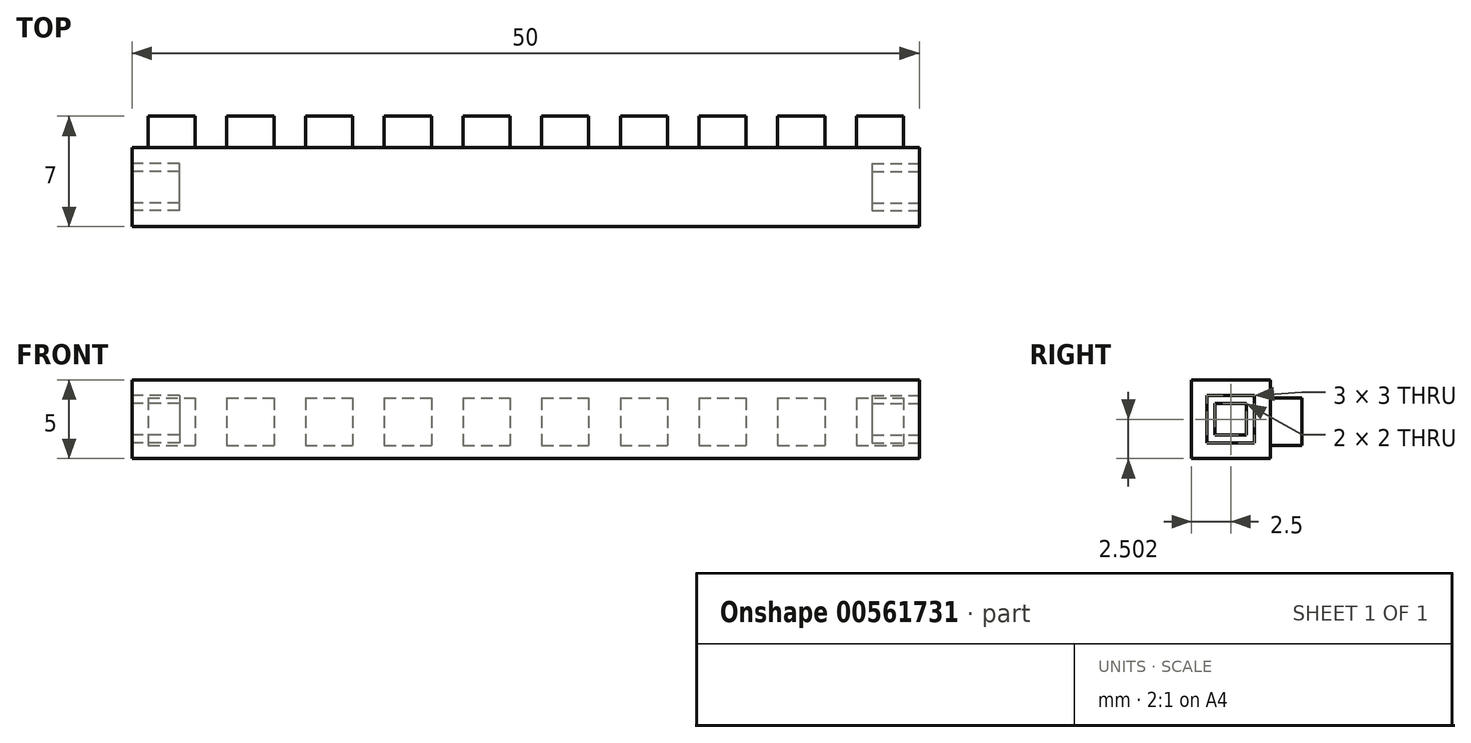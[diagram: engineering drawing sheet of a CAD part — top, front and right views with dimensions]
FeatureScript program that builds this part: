
annotation { "Feature Type Name" : "Feature", "Feature Type Description" : "" }
export const myFeature = defineFeature(function(context is Context, id is Id, definition is map)
    precondition{}
    {
        {
            var Q0;
            Q0=qCreatedBy(makeId("Front.planeOp"),FACE);
            var sketch = newSketch(context, id + "F0", { "sketchPlane" : qUnion([Q0])});
            skLineSegment(sketch, "E0", {"start": v(-35.48, 11.23) * mm, "end": v(-35.48, 6.23) * mm});
            skLineSegment(sketch, "E1", {"start": v(-35.48, 6.23) * mm, "end": v(14.52, 6.23) * mm});
            skLineSegment(sketch, "E2", {"start": v(14.52, 6.23) * mm, "end": v(14.52, 11.23) * mm});
            skLineSegment(sketch, "E3", {"start": v(14.52, 11.23) * mm, "end": v(-35.48, 11.23) * mm});
            skSolve(sketch);
        }
        {
            var Q0;
            Q0=makeQuery(id+"F0.imprint","IMPRINT",FACE,{"disambiguationData":[TD([[makeQuery(id+"F0.imprint","IMPRINT",EDGE,{"derivedFrom":sQuery(id+"F0.wireOp",EDGE,"E0")}),1.0]])]});
            extrude(context, id + "F1", {"entities" : qUnion([Q0]), "depth" : 5 * mm, "offsetDistance" : 25 * mm});
        }
        {
            var Q0;
            Q0=qCreatedBy(makeId("Front.planeOp"),FACE);
            var sketch = newSketch(context, id + "F2", { "sketchPlane" : qUnion([Q0])});
            skLineSegment(sketch, "E4.bottom", {"start": v(-34.48, 10.09) * mm, "end": v(-31.48, 10.09) * mm});
            skLineSegment(sketch, "E4.top", {"start": v(-34.48, 7.09) * mm, "end": v(-31.48, 7.09) * mm});
            skLineSegment(sketch, "E4.left", {"start": v(-34.48, 10.09) * mm, "end": v(-34.48, 7.09) * mm});
            skLineSegment(sketch, "E4.right", {"start": v(-31.48, 10.09) * mm, "end": v(-31.48, 7.09) * mm});
            skPoint(sketch, "E4.middle", {"position": v(-32.98, 8.59) * mm});
            skLineSegment(sketch, "E5.1.0.0", {"start": v(-29.48, 10.09) * mm, "end": v(-26.48, 10.09) * mm});
            skLineSegment(sketch, "E5.1.0.1", {"start": v(-29.48, 10.09) * mm, "end": v(-29.48, 7.09) * mm});
            skLineSegment(sketch, "E5.1.0.2", {"start": v(-29.48, 7.09) * mm, "end": v(-26.48, 7.09) * mm});
            skLineSegment(sketch, "E5.1.0.3", {"start": v(-26.48, 10.09) * mm, "end": v(-26.48, 7.09) * mm});
            skLineSegment(sketch, "E5.2.0.0", {"start": v(-24.48, 10.09) * mm, "end": v(-21.48, 10.09) * mm});
            skLineSegment(sketch, "E5.2.0.1", {"start": v(-24.48, 10.09) * mm, "end": v(-24.48, 7.09) * mm});
            skLineSegment(sketch, "E5.2.0.2", {"start": v(-24.48, 7.09) * mm, "end": v(-21.48, 7.09) * mm});
            skLineSegment(sketch, "E5.2.0.3", {"start": v(-21.48, 10.09) * mm, "end": v(-21.48, 7.09) * mm});
            skLineSegment(sketch, "E5.3.0.0", {"start": v(-19.48, 10.09) * mm, "end": v(-16.48, 10.09) * mm});
            skLineSegment(sketch, "E5.3.0.1", {"start": v(-19.48, 10.09) * mm, "end": v(-19.48, 7.09) * mm});
            skLineSegment(sketch, "E5.3.0.2", {"start": v(-19.48, 7.09) * mm, "end": v(-16.48, 7.09) * mm});
            skLineSegment(sketch, "E5.3.0.3", {"start": v(-16.48, 10.09) * mm, "end": v(-16.48, 7.09) * mm});
            skLineSegment(sketch, "E5.4.0.0", {"start": v(-14.48, 10.09) * mm, "end": v(-11.48, 10.09) * mm});
            skLineSegment(sketch, "E5.4.0.1", {"start": v(-14.48, 10.09) * mm, "end": v(-14.48, 7.09) * mm});
            skLineSegment(sketch, "E5.4.0.2", {"start": v(-14.48, 7.09) * mm, "end": v(-11.48, 7.09) * mm});
            skLineSegment(sketch, "E5.4.0.3", {"start": v(-11.48, 10.09) * mm, "end": v(-11.48, 7.09) * mm});
            skLineSegment(sketch, "E5.5.0.0", {"start": v(-9.48, 10.09) * mm, "end": v(-6.48, 10.09) * mm});
            skLineSegment(sketch, "E5.5.0.1", {"start": v(-9.48, 10.09) * mm, "end": v(-9.48, 7.09) * mm});
            skLineSegment(sketch, "E5.5.0.2", {"start": v(-9.48, 7.09) * mm, "end": v(-6.48, 7.09) * mm});
            skLineSegment(sketch, "E5.5.0.3", {"start": v(-6.48, 10.09) * mm, "end": v(-6.48, 7.09) * mm});
            skLineSegment(sketch, "E5.6.0.0", {"start": v(-4.48, 10.09) * mm, "end": v(-1.48, 10.09) * mm});
            skLineSegment(sketch, "E5.6.0.1", {"start": v(-4.48, 10.09) * mm, "end": v(-4.48, 7.09) * mm});
            skLineSegment(sketch, "E5.6.0.2", {"start": v(-4.48, 7.09) * mm, "end": v(-1.48, 7.09) * mm});
            skLineSegment(sketch, "E5.6.0.3", {"start": v(-1.48, 10.09) * mm, "end": v(-1.48, 7.09) * mm});
            skLineSegment(sketch, "E5.7.0.0", {"start": v(0.52, 10.09) * mm, "end": v(3.52, 10.09) * mm});
            skLineSegment(sketch, "E5.7.0.1", {"start": v(0.52, 10.09) * mm, "end": v(0.52, 7.09) * mm});
            skLineSegment(sketch, "E5.7.0.2", {"start": v(0.52, 7.09) * mm, "end": v(3.52, 7.09) * mm});
            skLineSegment(sketch, "E5.7.0.3", {"start": v(3.52, 10.09) * mm, "end": v(3.52, 7.09) * mm});
            skLineSegment(sketch, "E5.8.0.0", {"start": v(5.52, 10.09) * mm, "end": v(8.52, 10.09) * mm});
            skLineSegment(sketch, "E5.8.0.1", {"start": v(5.52, 10.09) * mm, "end": v(5.52, 7.09) * mm});
            skLineSegment(sketch, "E5.8.0.2", {"start": v(5.52, 7.09) * mm, "end": v(8.52, 7.09) * mm});
            skLineSegment(sketch, "E5.8.0.3", {"start": v(8.52, 10.09) * mm, "end": v(8.52, 7.09) * mm});
            skLineSegment(sketch, "E5.9.0.0", {"start": v(10.52, 10.09) * mm, "end": v(13.52, 10.09) * mm});
            skLineSegment(sketch, "E5.9.0.1", {"start": v(10.52, 10.09) * mm, "end": v(10.52, 7.09) * mm});
            skLineSegment(sketch, "E5.9.0.2", {"start": v(10.52, 7.09) * mm, "end": v(13.52, 7.09) * mm});
            skLineSegment(sketch, "E5.9.0.3", {"start": v(13.52, 10.09) * mm, "end": v(13.52, 7.09) * mm});
            skLineSegment(sketch, "E5.direction1", {"start": v(-34.48, 10.09) * mm, "end": v(-29.48, 10.09) * mm, "construction": true});
            skSolve(sketch);
        }
        {
            var Q0;
            Q0 = qSketchRegion(id + "F2", true);
            extrude(context, id + "F3", {"entities" : qUnion([Q0]), "operationType" : NewBodyOperationType.ADD, "oppositeDirection" : true, "depth" : 2 * mm, "offsetDistance" : 25 * mm});
        }
        {
            var Q0;
            Q0=makeQuery(id+"F1.opExtrude","SWEPT_FACE",FACE,{"disambiguationData":[OSD([sQuery(id+"F0.wireOp",EDGE,"E0")])]});
            var sketch = newSketch(context, id + "F4", { "sketchPlane" : qUnion([Q0])});
            skLineSegment(sketch, "E6.bottom", {"start": v(3.5, 9.73) * mm, "end": v(1.5, 9.73) * mm});
            skLineSegment(sketch, "E6.top", {"start": v(3.5, 7.73) * mm, "end": v(1.5, 7.73) * mm});
            skLineSegment(sketch, "E6.left", {"start": v(3.5, 9.73) * mm, "end": v(3.5, 7.73) * mm});
            skLineSegment(sketch, "E6.right", {"start": v(1.5, 9.73) * mm, "end": v(1.5, 7.73) * mm});
            skPoint(sketch, "E6.middle", {"position": v(2.5, 8.73) * mm});
            skPoint(sketch, "E6.middle.positionSnap0", {"position": v(2.5, 11.23) * mm});
            skPoint(sketch, "E6.middle.positionSnap1", {"position": v(5, 8.73) * mm});
            skPoint(sketch, "E6.centerSnap0", {"position": v(2.5, 11.23) * mm});
            skPoint(sketch, "E6.centerSnap1", {"position": v(5, 8.73) * mm});
            skLineSegment(sketch, "E7.bottom", {"start": v(4, 10.23) * mm, "end": v(1, 10.23) * mm});
            skLineSegment(sketch, "E7.top", {"start": v(4, 7.23) * mm, "end": v(1, 7.23) * mm});
            skLineSegment(sketch, "E7.left", {"start": v(4, 10.23) * mm, "end": v(4, 7.23) * mm});
            skLineSegment(sketch, "E7.right", {"start": v(1, 10.23) * mm, "end": v(1, 7.23) * mm});
            skSolve(sketch);
        }
        {
            var Q0;
            Q0=makeQuery(id+"F4.imprint","IMPRINT",FACE,{"disambiguationData":[TD([[makeQuery(id+"F4.imprint","IMPRINT",EDGE,{"derivedFrom":sQuery(id+"F4.wireOp",EDGE,"E6.bottom")}),-1.0]])]});
            extrude(context, id + "F5", {"entities" : qUnion([Q0]), "operationType" : NewBodyOperationType.REMOVE, "oppositeDirection" : true, "depth" : 3 * mm, "offsetDistance" : 25 * mm});
        }
        {
            var Q0;
            Q0=makeQuery(id+"F1.opExtrude","SWEPT_FACE",FACE,{"disambiguationData":[OSD([sQuery(id+"F0.wireOp",EDGE,"E2")])]});
            var sketch = newSketch(context, id + "F6", { "sketchPlane" : qUnion([Q0])});
            skLineSegment(sketch, "E8.bottom", {"start": v(-1, 10.23) * mm, "end": v(-4, 10.23) * mm});
            skLineSegment(sketch, "E8.top", {"start": v(-1, 7.23) * mm, "end": v(-4, 7.23) * mm});
            skLineSegment(sketch, "E8.left", {"start": v(-1, 10.23) * mm, "end": v(-1, 7.23) * mm});
            skLineSegment(sketch, "E8.right", {"start": v(-4, 10.23) * mm, "end": v(-4, 7.23) * mm});
            skPoint(sketch, "E8.middle", {"position": v(-2.5, 8.73) * mm});
            skPoint(sketch, "E8.middle.positionSnap0", {"position": v(0, 8.73) * mm});
            skPoint(sketch, "E8.middle.positionSnap1", {"position": v(-2.5, 11.23) * mm});
            skPoint(sketch, "E8.centerSnap0", {"position": v(0, 8.73) * mm});
            skPoint(sketch, "E8.centerSnap1", {"position": v(-2.5, 11.23) * mm});
            skLineSegment(sketch, "E9.bottom", {"start": v(-1.5, 9.73) * mm, "end": v(-3.5, 9.73) * mm});
            skLineSegment(sketch, "E9.top", {"start": v(-1.5, 7.73) * mm, "end": v(-3.5, 7.73) * mm});
            skLineSegment(sketch, "E9.left", {"start": v(-1.5, 9.73) * mm, "end": v(-1.5, 7.73) * mm});
            skLineSegment(sketch, "E9.right", {"start": v(-3.5, 9.73) * mm, "end": v(-3.5, 7.73) * mm});
            skSolve(sketch);
        }
        {
            var Q0;
            Q0 = qSketchRegion(id + "F6", true);
            extrude(context, id + "F7", {"entities" : qUnion([Q0]), "operationType" : NewBodyOperationType.REMOVE, "oppositeDirection" : true, "depth" : 3 * mm, "offsetDistance" : 25 * mm});
        }
    });
